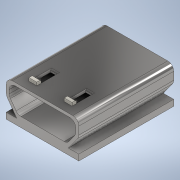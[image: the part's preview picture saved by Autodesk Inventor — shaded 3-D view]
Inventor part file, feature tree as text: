
AUTODESK INVENTOR PART (.ipt)
format: ipt  version: 2020 (Build 240168000, 168)  size: 289,792 bytes
history: native  units: in
note: dims shown in document units (in); Inventor stores cm internally (conversion verified against a paired STEP export)
features: extrude x7, sketch x3, chamfer x3
ambient origin geometry x8: Origin, YZ Plane, XZ Plane, XY Plane, X Axis, Y Axis, Z Axis, Center Point
bodies: Solid1 (feature_tree)
feature tree (13):
  extrude  "Extrusion1"  Depth=0.4719in
  sketch  "Sketch2"  dims[d3=0.2362in d4=0.0in d7=0.0394in]
  extrude  "Extrusion2"  Depth=0.0394in
  extrude  "Extrusion3"  Depth=0.0394in
  extrude  "Extrusion4"  Depth=0.0394in
  extrude  "Extrusion5"  Depth=0.0394in
  sketch  "Sketch3"  dims[d8=0.0394in d9=0.0394in d12=0.0394in d14=0.0394in d16=0.0394in d18=0.0394in d19=0.0394in d20=0.0394in d21=3.5433in d23=0.0394in d24=0.3937in d26=0.3937in d28=0.6299in d29=0.0in d30=0.5512in d31=0.0in d32=0.1575in d33=0.0in d34=0.1181in d35=0.0in d38=0.0512in d40=0.0512in d41=0.0394in d42=0.0in d43=0.0197in d44=0.0in d45=0.0079in d46=0.0787in d47=45.0deg d48=0.0079in d49=0.0787in d50=45.0deg d51=0.0079in d52=0.0787in d53=45.0deg]
  extrude  "Extrusion6"  Depth=0.0394in
  extrude  "Extrusion7"  Depth=0.0394in
  chamfer  "Chamfer1"  Distance=0.0394in
  chamfer  "Chamfer2"  Distance=0.0394in
  chamfer  "Chamfer3"  Distance=0.0394in
  sketch  "Sketch1"  dims[d1=0.6172in d2=0.4719in]
